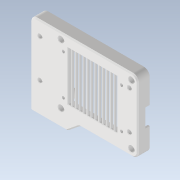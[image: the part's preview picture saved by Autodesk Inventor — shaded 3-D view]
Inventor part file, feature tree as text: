
AUTODESK INVENTOR PART (.ipt)
format: ipt  version: 2022.1 (Build 261234020, 234B)  size: 698,368 bytes
history: native  units: mm
features: reference x58, extrude x12, sketch x12, other x12, projected_geometry x7, chamfer x6, hole x3, fillet x3, direct_edit x1, move_body x1
ambient origin geometry x8: Origin, YZ Plane, XZ Plane, XY Plane, X Axis, Y Axis, Z Axis, Center Point
bodies: Volumenkörper1 (feature_tree)
feature tree (115):
  extrude  "Extrusion1"  Depth=7.1mm
  extrude  "Extrusion2"  Depth=7.1mm
  extrude  "Extrusion3"  Depth=7.1mm
  extrude  "Extrusion4"  Depth=7.1mm
  sketch  "Skizze5"  dims[d8=3.8mm d9=0.0mm d11=55.755667mm]
  hole  "Bohrung1"  [1 undecoded]
  hole  "Bohrung2"  [1 undecoded]
  hole  "Bohrung3"  [1 undecoded]
  chamfer  "Fase1"  Distance=1.6mm
  chamfer  "Fase2"  Distance=1.6mm
  extrude  "Extrusion5"  Depth=1.6mm
  extrude  "Extrusion6"  Depth=1.6mm
  extrude  "Extrusion7"  Depth=5.0mm TaperAngle=0.0deg
  fillet  "Rundung1"  Radius=40.4mm
  fillet  "Rundung2"  Radius=40.4mm
  extrude  "Extrusion8"  TaperAngle=0.0deg  [1 undecoded]
  extrude  "Extrusion10"  Depth=1.2mm
  direct_edit  "Direktbearbeitung1"
  chamfer  "Fase4"  Distance=1.2mm
  chamfer  "Fase5"  Distance=1.2mm
  extrude  "Extrusion11"  Depth=1.2mm
  chamfer  "Fase6"  Distance=1.2mm
  extrude  "Extrusion12"  Depth=1.2mm
  fillet  "Rundung4"  Radius=1.2mm
  chamfer  "Fase7"  Distance=1.2mm
  sketch  "Skizze1"  dims[d0=7.1mm d1=7.1mm]
  reference  "Referenz1"
  reference  "Referenz2"
  reference  "Referenz3"
  reference  "Referenz4"
  reference  "Referenz5"
  reference  "Referenz6"
  reference  "Referenz7"
  reference  "Referenz8"
  sketch  "Skizze2"  dims[d2=7.1mm d3=7.1mm]
  reference  "Referenz9"
  reference  "Referenz10"
  reference  "Referenz11"
  reference  "Referenz12"
  reference  "Referenz13"
  reference  "Referenz14"
  reference  "Referenz15"
  reference  "Referenz16"
  reference  "Referenz17"
  reference  "Referenz18"
  reference  "Referenz19"
  reference  "Referenz20"
  reference  "Referenz21"
  reference  "Referenz22"
  reference  "Referenz23"
  reference  "Referenz24"
  reference  "Referenz25"
  reference  "Referenz26"
  reference  "Referenz27"
  reference  "Referenz28"
  reference  "Referenz29"
  reference  "Referenz30"
  reference  "Referenz31"
  reference  "Referenz32"
  reference  "Referenz33"
  reference  "Referenz34"
  reference  "Referenz35"
  reference  "Referenz36"
  reference  "Referenz37"
  reference  "Referenz38"
  reference  "Referenz39"
  reference  "Referenz40"
  reference  "Referenz41"
  reference  "Referenz42"
  reference  "Referenz43"
  reference  "Referenz44"
  reference  "Referenz45"
  reference  "Referenz46"
  reference  "Referenz47"
  reference  "Referenz48"
  reference  "Referenz49"
  reference  "Referenz50"
  reference  "Referenz51"
  reference  "Referenz52"
  sketch  "Skizze3"  dims[d4=7.1mm d5=7.1mm]
  projected_geometry  "Projizierte Kontur1"
  reference  "Referenz53"
  sketch  "Skizze4"  dims[d6=7.1mm d7=7.1mm]
  projected_geometry  "Projizierte Kontur2"
  sketch  "Skizze6"  dims[d12=84.755666mm d13=0.4mm]
  sketch  "Skizze7"  dims[d14=0.4mm d15=85.555667mm]
  projected_geometry  "Projizierte Kontur3"
  sketch  "Skizze8"  dims[d16=0.3mm]
  sketch  "Skizze9"  dims[d17=0.3mm]
  projected_geometry  "Projizierte Kontur4"
  sketch  "Skizze10"  dims[d18=56.355667mm]
  reference  "Referenz54"
  projected_geometry  "Projizierte Kontur5"
  reference  "Referenz58"
  sketch  "Skizze13"  dims[d19=3.4mm]
  reference  "Referenz59"
  projected_geometry  "Projizierte Kontur7"
  reference  "Referenz60"
  reference  "Referenz63"
  sketch  "Skizze14"  dims[d20=1.6mm d21=1.6mm d22=1.6mm d23=1.6mm d25=1.6mm d26=5.0mm d27=0.0mm d28=40.4mm d29=40.4mm d38=0.0mm d39=1.2mm d40=1.2mm d41=1.2mm d42=1.2mm d43=1.2mm d44=1.2mm d45=1.2mm d46=1.2mm d47=1.2mm d48=1.2mm d49=1.2mm d54=3.2mm d55=3.2mm d56=3.2mm d57=3.2mm d58=3.2mm d59=3.2mm d60=3.2mm d61=3.2mm d62=3.2mm d63=3.2mm d64=1.2mm d65=3.2mm d66=2.0mm d67=2.0mm d69=3.8mm d70=3.8mm d71=2.6mm d72=0.0mm d73=2.2mm d74=0.0mm d75=3.3mm d76=6.0mm d77=4.7mm d78=5.0mm d79=90.0deg d80=8.0mm d81=0.0mm d82=2.5mm d83=6.0mm d84=4.7mm d85=5.0mm d86=90.0deg d87=8.0mm d88=0.0mm d89=31.5mm d91=7.0mm d92=8.0mm d93=2.4mm d94=3.3mm d95=6.0mm d96=5.8mm d97=3.2mm d98=90.0deg d99=8.0mm d100=20.594885mm d101=0.4mm d102=2.0mm d103=45.0deg d104=0.4mm d105=2.0mm d106=45.0deg d107=8.0mm d108=29.6mm d109=1.6mm d110=1.6mm d111=1.8mm d112=3.2mm d113=0.0mm d114=1.6mm d115=17.4mm d116=4.8mm d117=4.4mm d118=0.0mm d119=0.0mm d120=10.0mm d121=0.0mm d122=3.0mm d123=1.6mm d127=10.0mm d128=0.0mm d131=10.0mm d132=0.0mm d134=0.0mm d135=0.0mm d136=-1.0mm d137=1.0mm d138=2.0mm d139=45.0deg d140=0.6mm d141=2.0mm d142=45.0deg d143=0.3mm d144=0.3mm d145=2.6mm d146=0.0mm d147=1.2mm d148=2.0mm d149=45.0deg d150=3.0mm d151=4.6mm d152=1.6mm d153=10.0mm d154=0.0mm d155=3.0mm d156=0.4mm d157=2.0mm d158=45.0deg]
  projected_geometry  "Projizierte Kontur8"
  other  "<userpath>\Desktop\CM4Case\000_CM4-IO-BASE.iam"
  other  "000_CM4-IO-BASE.iam"
  other  "CM4-step:1"
  other  "Shapes"
  other  "Dielectric"
  other  "Dielectric_4"
  other  "Board_1"
  other  "<userpath>\Desktop\GitHub\Voron-2-Mods\Arducam_IMX477_CM4\CM4\CAD\CM4_Case.iam"
  other  "CM4_Case.iam"
  other  "CM4_Case_Top:1"
  move_body  "Verschieben1"
  other  "000_CM4-IO-BASE:1"
  other  "TF1_285"
  extrude  "Extruded_283"  Depth=1.2mm
note: 4 required parameter values undecoded (feature->parameter linkage not recoverable at this tier; creation-order binding heuristic only, values carry confidence <= 0.55)
